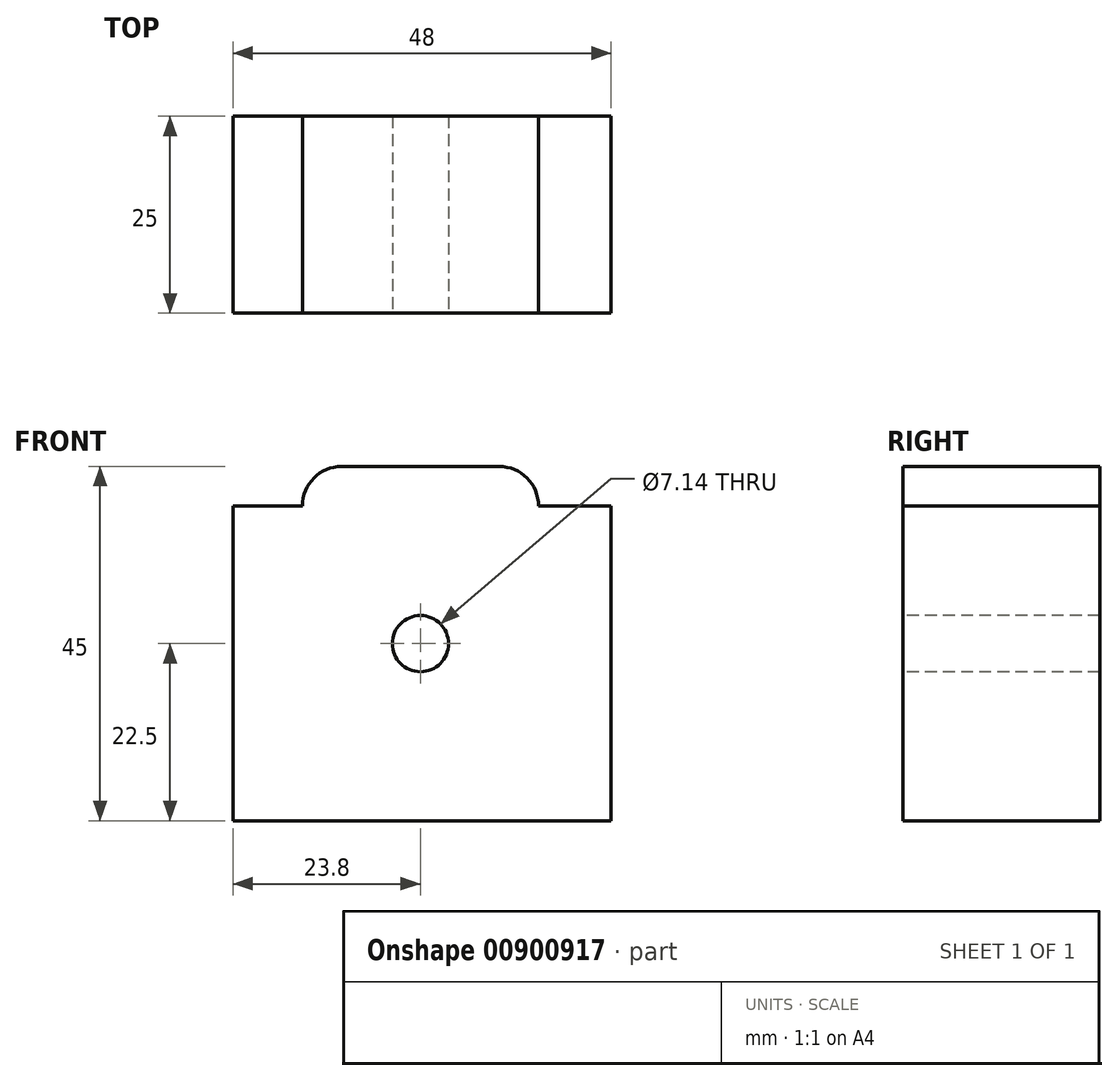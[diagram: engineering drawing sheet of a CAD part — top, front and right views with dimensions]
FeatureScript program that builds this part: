
annotation { "Feature Type Name" : "Feature", "Feature Type Description" : "" }
export const myFeature = defineFeature(function(context is Context, id is Id, definition is map)
    precondition{}
    {
        {
            var Q0;
            Q0=qCreatedBy(makeId("Front.planeOp"),FACE);
            var sketch = newSketch(context, id + "F0", { "sketchPlane" : qUnion([Q0])});
            skLineSegment(sketch, "E0.bottom", {"start": v(0, 0) * mm, "end": v(30, 0) * mm});
            skLineSegment(sketch, "E0.top", {"start": v(0, 45) * mm, "end": v(30, 45) * mm});
            skLineSegment(sketch, "E0.left", {"start": v(0, 0) * mm, "end": v(0, 45) * mm});
            skLineSegment(sketch, "E0.right", {"start": v(30, 0) * mm, "end": v(30, 45) * mm});
            skSolve(sketch);
        }
        {
            var Q0;
            Q0=makeQuery(id+"F0.imprint","IMPRINT",FACE,{"disambiguationData":[TD([[makeQuery(id+"F0.imprint","IMPRINT",EDGE,{"derivedFrom":sQuery(id+"F0.wireOp",EDGE,"E0.bottom")}),1.0]])]});
            extrude(context, id + "F1", {"entities" : qUnion([Q0]), "depth" : 25 * mm, "offsetDistance" : 25 * mm});
        }
        {
            var Q0;
            Q0=makeQuery(id+"F1.opExtrude","CAP_FACE",FACE,{"disambiguationData":[OSD([sQuery(id+"F0.wireOp",EDGE,"E0.bottom"),sQuery(id+"F0.wireOp",EDGE,"E0.top"),sQuery(id+"F0.wireOp",EDGE,"E0.left"),sQuery(id+"F0.wireOp",EDGE,"E0.right")])],"isStart":false});
            var sketch = newSketch(context, id + "F2", { "sketchPlane" : qUnion([Q0])});
            skPoint(sketch, "E1", {"position": v(15, 22.5) * mm});
            skSolve(sketch);
        }
        {
            var Q0;
            Q0=sQuery(id+"F2.wireOp",VERTEX,"E1");
            var Q1;
            Q1=makeQuery(id+"F1.opExtrude","SWEPT_BODY",BODY,{"disambiguationData":[OSD([sQuery(id+"F0.wireOp",EDGE,"E0.bottom"),sQuery(id+"F0.wireOp",EDGE,"E0.top"),sQuery(id+"F0.wireOp",EDGE,"E0.left"),sQuery(id+"F0.wireOp",EDGE,"E0.right")])]});
            hole(context, id + "F3", {"style" : HoleStyle.SIMPLE, "endStyle" : HoleEndStyle.THROUGH, "standardTappedOrClearance" : lookupTablePath({ "fit" : "Normal (ASME)", "standard" : "ANSI", "size" : "1/4", "type" : "Clearance" }), "standardBlindInLast" : lookupTablePath({ "fit" : "Normal", "standard" : "ANSI", "size" : "1/4", "type" : "Clearance" }), "holeDiameter" : 7.14 * mm, "majorDiameter" : 5 * mm, "isTappedThrough" : true, "tappedDepth" : 12 * mm, "tapClearance" : 3, "locations" : qUnion([Q0]), "scope" : qUnion([Q1])});
        }
        {
            var Q0;
            Q0=makeQuery(id+"F1.opExtrude","SWEPT_EDGE",EDGE,{"disambiguationData":[OSD([sQuery(id+"F0.wireOp",EDGE,"E0.top"),sQuery(id+"F0.wireOp",EDGE,"E0.right")])]});
            var Q1;
            Q1=makeQuery(id+"F1.opExtrude","SWEPT_EDGE",EDGE,{"disambiguationData":[OSD([sQuery(id+"F0.wireOp",EDGE,"E0.top"),sQuery(id+"F0.wireOp",EDGE,"E0.left")])]});
            fillet(context, id + "F4", {"entities" : qUnion([Q0, Q1]), "radius" : 5 * mm, "tangentPropagation" : true, "allowEdgeOverflow" : false});
        }
        {
            var Q0;
            Q0=makeQuery(id+"F1.opExtrude","SWEPT_FACE",FACE,{"disambiguationData":[OSD([sQuery(id+"F0.wireOp",EDGE,"E0.right")])]});
            extrude(context, id + "F5", {"entities" : qUnion([Q0]), "operationType" : NewBodyOperationType.ADD, "depth" : 9.2 * mm, "offsetDistance" : 25 * mm});
        }
        {
            var Q0;
            Q0=makeQuery(id+"F1.opExtrude","SWEPT_FACE",FACE,{"disambiguationData":[OSD([sQuery(id+"F0.wireOp",EDGE,"E0.left")])]});
            extrude(context, id + "F6", {"entities" : qUnion([Q0]), "operationType" : NewBodyOperationType.ADD, "depth" : 8.8 * mm, "offsetDistance" : 25 * mm});
        }
    });
